# Revit family: ROTHOB_Rothoblaas_Screw_VGSA4
name_source: partatom
category: Structural Connections
units: mm (PartAtom-declared; Revit-internal decimal feet)

## family parameters
Cut with Voids When Loaded = No
Enable cutting in views = Yes
Host = Face
Material for Model Behavior = Steel
OmniClass Number = 23.20.40.11.14.24
OmniClass Title = Screws
Shared = No

## types (16) — shared parameters
AssetType = Fixed
BIMObjectName = ROTHOB_Rothoblaas_Screw_VGSA4
CECode = ETA-11/0030
CETitle = Rotho Blaas Self-tapping screws and threaded rods
Category = Pr_20_29_76_75: Self-tapping screws
CodePerformance = CE - Construction products
Color = Silver
Default Elevation = 1219.2 mm
Description = Full thread connector with countersunk head
DurationUnit = Years
Esporta tipo in formato IFC con nome = IfcMechanicalFastenerType
ExpectedLife = 50
Features = Self-tapping screws for timber constructions
Finish = Stainless steel
H1 = 0.9145 mm  [stored 0.00300033 ft]
H5 = 1 mm  [stored 0.00328084 ft]
HeadAngle = 90.000°
HeadType = Countersunk head with ribs
ICC-ESCode = ESR-4645 / ELC-4645
ICC-ESTitle = Rotho blaas self-tapping wood screws / Rotho Blaas Self-tapping Wood Screws
IfcExportAs = IfcMechanicalFastenerType
IfcExportType = USERDEFINED
ManufacturerName = ROTHO BLAAS SRL
ManufacturerURL = www.rothoblaas.com
Material = A4 | AISI316 austenitic stainless steel (CRC III)
ModelDisclaimer = The latest version of the data sheets can be found on our website
Name = Screw
ObjectMaterial = ROTHOB_Rothoblaas_StainlessSteelAISI316
OmniClassCode = 23.20.40.11.14.24
OmniClassTitle = Screws
OmniClassVersion = 2012-05-16
ProductInformation = www.rothoblaas.com/products/new-products/vgs-a4
Revision = 000
Shape = Cylindrical
Tipo IFC predefinito = USERDEFINED
UniClass2015Code = Pr_20_29_76_75
UniClass2015Title = Self-tapping screws
UniClass2015Version = Products v1.38
Version = 001

## per-type parameters (varying)
| type | BitType | GTIN | H2 | H3 | H4 | HeadDiameter_dk | HeadThickness_t1 | InnerHeadDiameter | InsertionLength_L | MinWeight | ModelNumber | ModelNumberCode | NominalDiameter | NominalDiameter_d1 | NominalLength | Size | ThreadDiameter_d2 | ThreadLength_b | TipLength | UnderheadDiameter |
| 9120_9x120mm | 40 | 8059386076903 | 1.727 mm  [stored 0.00566601 ft] | 2.8585 mm  [stored 0.00937828 ft] | 5.02 mm  [stored 0.0164698 ft] | 16 mm  [stored 0.0524934 ft] | 6.5 mm | 10.925 mm  [stored 0.0358432 ft] | 120 mm  [stored 0.393701 ft] | 0.033 kg | VGS9120A4 | 9120 | 9 mm  [stored 0.0295276 ft] | 9 mm  [stored 0.0295276 ft] | 120 mm  [stored 0.393701 ft] | 9x120 mm | 5.9 mm  [stored 0.019357 ft] | 110 mm  [stored 0.360892 ft] | 10.8235 mm  [stored 0.0355102 ft] | 6.5 mm |
| 11100_11x100mm | 50 | 8059386077016 | 3.5721 mm | 3.7134 mm  [stored 0.0121831 ft] | 1.8 mm  [stored 0.00590551 ft] | 19.3 mm | 8.2 mm  [stored 0.0269029 ft] | 10.577 mm  [stored 0.0347014 ft] | 100 mm  [stored 0.328084 ft] | 0.040 kg | VGS11100A4 | 11100 | 11 mm  [stored 0.0360892 ft] | 11 mm  [stored 0.0360892 ft] | 100 mm  [stored 0.328084 ft] | 11x100 mm | 6.6 mm  [stored 0.0216535 ft] | 90 mm  [stored 0.295276 ft] | 9.9216 mm  [stored 0.0325512 ft] | 7.7 mm  [stored 0.0252625 ft] |
| 9280_9x280mm | 40 | 8059386077146 | 1.727 mm  [stored 0.00566601 ft] | 2.8585 mm  [stored 0.00937828 ft] | 5.02 mm  [stored 0.0164698 ft] | 16 mm  [stored 0.0524934 ft] | 6.5 mm | 10.925 mm  [stored 0.0358432 ft] | 280 mm  [stored 0.918635 ft] | 0.075 kg | VGS9280A4 | 9280 | 9 mm  [stored 0.0295276 ft] | 9 mm  [stored 0.0295276 ft] | 280 mm  [stored 0.918635 ft] | 9x280 mm | 5.9 mm  [stored 0.019357 ft] | 270 mm  [stored 0.885827 ft] | 1.7146 mm  [stored 0.00562533 ft] | 6.5 mm |
| 9160_9x160mm | 40 | 8059386076859 | 1.727 mm  [stored 0.00566601 ft] | 2.8585 mm  [stored 0.00937828 ft] | 5.02 mm  [stored 0.0164698 ft] | 16 mm  [stored 0.0524934 ft] | 6.5 mm | 10.925 mm  [stored 0.0358432 ft] | 160 mm  [stored 0.524934 ft] | 0.044 kg | VGS9160A4 | 9160 | 9 mm  [stored 0.0295276 ft] | 9 mm  [stored 0.0295276 ft] | 160 mm  [stored 0.524934 ft] | 9x160 mm | 5.9 mm  [stored 0.019357 ft] | 150 mm | 10.8235 mm  [stored 0.0355102 ft] | 6.5 mm |
| 9200_9x200mm | 40 | 8059386077153 | 1.727 mm  [stored 0.00566601 ft] | 2.8585 mm  [stored 0.00937828 ft] | 5.02 mm  [stored 0.0164698 ft] | 16 mm  [stored 0.0524934 ft] | 6.5 mm | 10.925 mm  [stored 0.0358432 ft] | 200 mm  [stored 0.656168 ft] | 0.054 kg | VGS9200A4 | 9200 | 9 mm  [stored 0.0295276 ft] | 9 mm  [stored 0.0295276 ft] | 200 mm  [stored 0.656168 ft] | 9x200 mm | 5.9 mm  [stored 0.019357 ft] | 190 mm | 10.8235 mm  [stored 0.0355102 ft] | 6.5 mm |
| 9240_9x240mm | 40 | 8059386076910 | 1.727 mm  [stored 0.00566601 ft] | 2.8585 mm  [stored 0.00937828 ft] | 5.02 mm  [stored 0.0164698 ft] | 16 mm  [stored 0.0524934 ft] | 6.5 mm | 10.925 mm  [stored 0.0358432 ft] | 240 mm  [stored 0.787402 ft] | 0.065 kg | VGS9240A4 | 9240 | 9 mm  [stored 0.0295276 ft] | 9 mm  [stored 0.0295276 ft] | 240 mm  [stored 0.787402 ft] | 9x240 mm | 5.9 mm  [stored 0.019357 ft] | 230 mm  [stored 0.754593 ft] | 10.8235 mm  [stored 0.0355102 ft] | 6.5 mm |
| 9320_9x320mm | 40 | 8059386076965 | 1.727 mm  [stored 0.00566601 ft] | 2.8585 mm  [stored 0.00937828 ft] | 5.02 mm  [stored 0.0164698 ft] | 16 mm  [stored 0.0524934 ft] | 6.5 mm | 10.925 mm  [stored 0.0358432 ft] | 320 mm | 0.088 kg | VGS9320A4 | 9320 | 9 mm  [stored 0.0295276 ft] | 9 mm  [stored 0.0295276 ft] | 320 mm | 9x320 mm | 5.9 mm  [stored 0.019357 ft] | 310 mm  [stored 1.01706 ft] | 1.7146 mm  [stored 0.00562533 ft] | 6.5 mm |
| 9360_9x360mm | 40 | 8059386077139 | 1.727 mm  [stored 0.00566601 ft] | 2.8585 mm  [stored 0.00937828 ft] | 5.02 mm  [stored 0.0164698 ft] | 16 mm  [stored 0.0524934 ft] | 6.5 mm | 10.925 mm  [stored 0.0358432 ft] | 360 mm | 0.098 kg | VGS9360A4 | 9360 | 9 mm  [stored 0.0295276 ft] | 9 mm  [stored 0.0295276 ft] | 360 mm | 9x360 mm | 5.9 mm  [stored 0.019357 ft] | 350 mm | 1.7146 mm  [stored 0.00562533 ft] | 6.5 mm |
| 11150_11x150mm | 50 | 8059386077184 | 3.5721 mm | 3.7134 mm  [stored 0.0121831 ft] | 1.8 mm  [stored 0.00590551 ft] | 19.3 mm | 8.2 mm  [stored 0.0269029 ft] | 10.577 mm  [stored 0.0347014 ft] | 150 mm | 0.057 kg | VGS11150A4 | 11150 | 11 mm  [stored 0.0360892 ft] | 11 mm  [stored 0.0360892 ft] | 150 mm | 11x150 mm | 6.6 mm  [stored 0.0216535 ft] | 140 mm  [stored 0.459318 ft] | 9.9216 mm  [stored 0.0325512 ft] | 7.7 mm  [stored 0.0252625 ft] |
| 11200_11x200mm | 50 | 8059386076866 | 3.5721 mm | 3.7134 mm  [stored 0.0121831 ft] | 1.8 mm  [stored 0.00590551 ft] | 19.3 mm | 8.2 mm  [stored 0.0269029 ft] | 10.577 mm  [stored 0.0347014 ft] | 200 mm  [stored 0.656168 ft] | 0.083 kg | VGS11200A4 | 11200 | 11 mm  [stored 0.0360892 ft] | 11 mm  [stored 0.0360892 ft] | 200 mm  [stored 0.656168 ft] | 11x200 mm | 6.6 mm  [stored 0.0216535 ft] | 190 mm | 9.9216 mm  [stored 0.0325512 ft] | 7.7 mm  [stored 0.0252625 ft] |
| 11250_11x250mm | 50 | 8059386077191 | 3.5721 mm | 3.7134 mm  [stored 0.0121831 ft] | 1.8 mm  [stored 0.00590551 ft] | 19.3 mm | 8.2 mm  [stored 0.0269029 ft] | 10.577 mm  [stored 0.0347014 ft] | 250 mm  [stored 0.82021 ft] | 0.093 kg | VGS11250A4 | 11250 | 11 mm  [stored 0.0360892 ft] | 11 mm  [stored 0.0360892 ft] | 250 mm  [stored 0.82021 ft] | 11x250 mm | 6.6 mm  [stored 0.0216535 ft] | 240 mm  [stored 0.787402 ft] | 9.9216 mm  [stored 0.0325512 ft] | 7.7 mm  [stored 0.0252625 ft] |
| 11300_11x300mm | 50 | 8059386076972 | 3.5721 mm | 3.7134 mm  [stored 0.0121831 ft] | 1.8 mm  [stored 0.00590551 ft] | 19.3 mm | 8.2 mm  [stored 0.0269029 ft] | 10.577 mm  [stored 0.0347014 ft] | 300 mm | 0.112 kg | VGS11300A4 | 11300 | 11 mm  [stored 0.0360892 ft] | 11 mm  [stored 0.0360892 ft] | 300 mm | 11x300 mm | 6.6 mm  [stored 0.0216535 ft] | 290 mm  [stored 0.951444 ft] | 1.8925 mm  [stored 0.00620899 ft] | 7.7 mm  [stored 0.0252625 ft] |
| 11350_11x350mm | 50 | 8059386076989 | 3.5721 mm | 3.7134 mm  [stored 0.0121831 ft] | 1.8 mm  [stored 0.00590551 ft] | 19.3 mm | 8.2 mm  [stored 0.0269029 ft] | 10.577 mm  [stored 0.0347014 ft] | 350 mm | 0.121 kg | VGS11350A4 | 11350 | 11 mm  [stored 0.0360892 ft] | 11 mm  [stored 0.0360892 ft] | 350 mm | 11x350 mm | 6.6 mm  [stored 0.0216535 ft] | 340 mm | 1.8925 mm  [stored 0.00620899 ft] | 7.7 mm  [stored 0.0252625 ft] |
| 11400_11x400mm | 50 | 8059386076873 | 3.5721 mm | 3.7134 mm  [stored 0.0121831 ft] | 1.8 mm  [stored 0.00590551 ft] | 19.3 mm | 8.2 mm  [stored 0.0269029 ft] | 10.577 mm  [stored 0.0347014 ft] | 400 mm | 0.148 kg | VGS11400A4 | 11400 | 11 mm  [stored 0.0360892 ft] | 11 mm  [stored 0.0360892 ft] | 400 mm | 11x400 mm | 6.6 mm  [stored 0.0216535 ft] | 390 mm | 1.8925 mm  [stored 0.00620899 ft] | 7.7 mm  [stored 0.0252625 ft] |
| 11500_11x500mm | 50 | 8059386076941 | 3.5721 mm | 3.7134 mm  [stored 0.0121831 ft] | 1.8 mm  [stored 0.00590551 ft] | 19.3 mm | 8.2 mm  [stored 0.0269029 ft] | 10.577 mm  [stored 0.0347014 ft] | 500 mm | 0.183 kg | VGS11500A4 | 11500 | 11 mm  [stored 0.0360892 ft] | 11 mm  [stored 0.0360892 ft] | 500 mm | 11x500 mm | 6.6 mm  [stored 0.0216535 ft] | 490 mm | 1.8925 mm  [stored 0.00620899 ft] | 7.7 mm  [stored 0.0252625 ft] |
| 11600_11x600mm | 50 | 8059386076958 | 3.5721 mm | 3.7134 mm  [stored 0.0121831 ft] | 1.8 mm  [stored 0.00590551 ft] | 19.3 mm | 8.2 mm  [stored 0.0269029 ft] | 10.577 mm  [stored 0.0347014 ft] | 600 mm | 0.219 kg | VGS11600A4 | 11600 | 11 mm  [stored 0.0360892 ft] | 11 mm  [stored 0.0360892 ft] | 600 mm | 11x600 mm | 6.6 mm  [stored 0.0216535 ft] | 590 mm | 1.8925 mm  [stored 0.00620899 ft] | 7.7 mm  [stored 0.0252625 ft] |

note: [stored X ft] marks values corroborated as IEEE doubles in the binary element streams (Revit-internal decimal feet)
